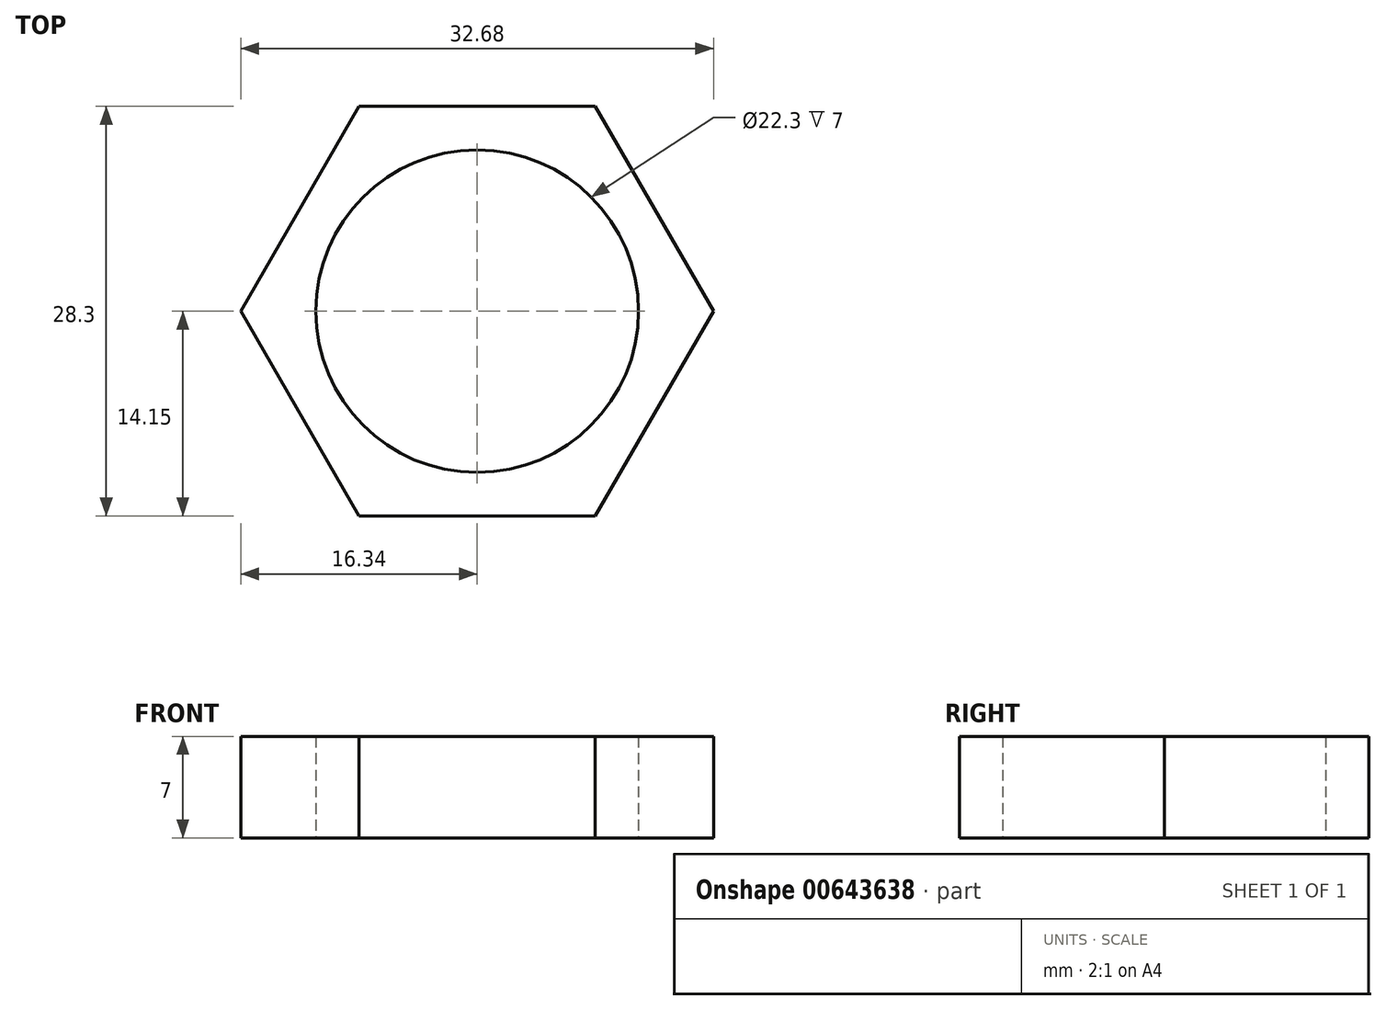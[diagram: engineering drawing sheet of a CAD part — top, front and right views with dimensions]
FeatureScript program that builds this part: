
annotation { "Feature Type Name" : "Feature", "Feature Type Description" : "" }
export const myFeature = defineFeature(function(context is Context, id is Id, definition is map)
    precondition{}
    {
        {
            var Q0;
            Q0=qCreatedBy(makeId("Top.planeOp"),FACE);
            var sketch = newSketch(context, id + "F0", { "sketchPlane" : qUnion([Q0])});
            skCircle(sketch, "E0", {"center": v(0, 0) * mm, "radius": 11.15 * mm});
            skLineSegment(sketch, "E1.0", {"start": v(-8.17, 14.15) * mm, "end": v(8.17, 14.15) * mm});
            skLineSegment(sketch, "E1.1", {"start": v(8.17, 14.15) * mm, "end": v(16.34, 0) * mm});
            skLineSegment(sketch, "E1.2", {"start": v(16.34, 0) * mm, "end": v(8.17, -14.15) * mm});
            skLineSegment(sketch, "E1.3", {"start": v(8.17, -14.15) * mm, "end": v(-8.17, -14.15) * mm});
            skLineSegment(sketch, "E1.4", {"start": v(-8.17, -14.15) * mm, "end": v(-16.34, 0) * mm});
            skLineSegment(sketch, "E1.5", {"start": v(-16.34, 0) * mm, "end": v(-8.17, 14.15) * mm});
            skPoint(sketch, "E1.0.midPoint", {"position": v(0, 14.15) * mm});
            skPoint(sketch, "E2", {"position": v(12.25, -7.07) * mm});
            skCircle(sketch, "E3.cCircle", {"center": v(24.5, -14.15) * mm, "radius": 14.15 * mm, "construction": true});
            skLineSegment(sketch, "E3.0", {"start": v(8.17, -14.15) * mm, "end": v(16.34, 0) * mm});
            skLineSegment(sketch, "E3.1", {"start": v(16.34, 0) * mm, "end": v(32.68, 0) * mm});
            skLineSegment(sketch, "E3.2", {"start": v(32.68, 0) * mm, "end": v(40.85, -14.15) * mm});
            skLineSegment(sketch, "E3.3", {"start": v(40.85, -14.15) * mm, "end": v(32.68, -28.3) * mm});
            skLineSegment(sketch, "E3.4", {"start": v(32.68, -28.3) * mm, "end": v(16.34, -28.3) * mm});
            skLineSegment(sketch, "E3.5", {"start": v(16.34, -28.3) * mm, "end": v(8.17, -14.15) * mm});
            skPoint(sketch, "E4", {"position": v(-12.25, -7.08) * mm});
            skCircle(sketch, "E5.cCircle", {"center": v(-24.5, -14.15) * mm, "radius": 14.15 * mm, "construction": true});
            skLineSegment(sketch, "E5.0", {"start": v(-16.34, 0) * mm, "end": v(-8.17, -14.15) * mm});
            skLineSegment(sketch, "E5.1", {"start": v(-8.17, -14.15) * mm, "end": v(-16.34, -28.3) * mm});
            skLineSegment(sketch, "E5.2", {"start": v(-16.34, -28.3) * mm, "end": v(-32.68, -28.3) * mm});
            skLineSegment(sketch, "E5.3", {"start": v(-32.68, -28.3) * mm, "end": v(-40.85, -14.15) * mm});
            skLineSegment(sketch, "E5.4", {"start": v(-40.85, -14.15) * mm, "end": v(-32.68, 0) * mm});
            skLineSegment(sketch, "E5.5", {"start": v(-32.68, 0) * mm, "end": v(-16.34, 0) * mm});
            skCircle(sketch, "E6.cCircle", {"center": v(0, 28.3) * mm, "radius": 14.15 * mm, "construction": true});
            skLineSegment(sketch, "E6.0", {"start": v(8.17, 14.15) * mm, "end": v(-8.17, 14.15) * mm});
            skLineSegment(sketch, "E6.1", {"start": v(-8.17, 14.15) * mm, "end": v(-16.34, 28.3) * mm});
            skLineSegment(sketch, "E6.2", {"start": v(-16.34, 28.3) * mm, "end": v(-8.17, 42.45) * mm});
            skLineSegment(sketch, "E6.3", {"start": v(-8.17, 42.45) * mm, "end": v(8.17, 42.45) * mm});
            skLineSegment(sketch, "E6.4", {"start": v(8.17, 42.45) * mm, "end": v(16.34, 28.3) * mm});
            skLineSegment(sketch, "E6.5", {"start": v(16.34, 28.3) * mm, "end": v(8.17, 14.15) * mm});
            skLineSegment(sketch, "E7", {"start": v(36.76, -21.23) * mm, "end": v(29.5, -17.03) * mm, "construction": true});
            skPoint(sketch, "E8.0.midPoint", {"position": v(36.76, -21.23) * mm});
            skLineSegment(sketch, "E9", {"start": v(0, 42.45) * mm, "end": v(0, 34.05) * mm, "construction": true});
            skPoint(sketch, "E10.0.midPoint", {"position": v(0, 42.45) * mm});
            skLineSegment(sketch, "E11", {"start": v(-36.76, -21.23) * mm, "end": v(-29.5, -17.03) * mm, "construction": true});
            skLineSegment(sketch, "E12.0", {"start": v(-33.15, -27.49) * mm, "end": v(-40.38, -14.96) * mm});
            skPoint(sketch, "E12.0.midPoint", {"position": v(-36.76, -21.23) * mm});
            skCircle(sketch, "E13.cCircle", {"center": v(0, 34.05) * mm, "radius": 8.4 * mm, "construction": true});
            skLineSegment(sketch, "E13.0", {"start": v(-4.85, 42.45) * mm, "end": v(4.85, 42.45) * mm});
            skLineSegment(sketch, "E13.1", {"start": v(4.85, 42.45) * mm, "end": v(9.7, 34.05) * mm});
            skLineSegment(sketch, "E13.2", {"start": v(9.7, 34.05) * mm, "end": v(4.85, 25.66) * mm});
            skLineSegment(sketch, "E13.3", {"start": v(4.85, 25.66) * mm, "end": v(-4.85, 25.66) * mm});
            skLineSegment(sketch, "E13.4", {"start": v(-4.85, 25.66) * mm, "end": v(-9.7, 34.05) * mm});
            skLineSegment(sketch, "E13.5", {"start": v(-9.7, 34.05) * mm, "end": v(-4.85, 42.45) * mm});
            skCircle(sketch, "E14.cCircle", {"center": v(29.5, -17.03) * mm, "radius": 8.4 * mm, "construction": true});
            skLineSegment(sketch, "E14.0", {"start": v(39.19, -17.03) * mm, "end": v(34.34, -25.42) * mm});
            skLineSegment(sketch, "E14.1", {"start": v(34.34, -25.42) * mm, "end": v(24.65, -25.42) * mm});
            skLineSegment(sketch, "E14.2", {"start": v(24.65, -25.42) * mm, "end": v(19.8, -17.03) * mm});
            skLineSegment(sketch, "E14.3", {"start": v(19.8, -17.03) * mm, "end": v(24.65, -8.63) * mm});
            skLineSegment(sketch, "E14.4", {"start": v(24.65, -8.63) * mm, "end": v(34.34, -8.63) * mm});
            skLineSegment(sketch, "E14.5", {"start": v(34.34, -8.63) * mm, "end": v(39.19, -17.03) * mm});
            skCircle(sketch, "E15.cCircle", {"center": v(-29.5, -17.03) * mm, "radius": 8.4 * mm, "construction": true});
            skLineSegment(sketch, "E15.0", {"start": v(-34.34, -25.42) * mm, "end": v(-39.19, -17.03) * mm});
            skLineSegment(sketch, "E15.1", {"start": v(-39.19, -17.03) * mm, "end": v(-34.34, -8.63) * mm});
            skLineSegment(sketch, "E15.2", {"start": v(-34.34, -8.63) * mm, "end": v(-24.65, -8.63) * mm});
            skLineSegment(sketch, "E15.3", {"start": v(-24.65, -8.63) * mm, "end": v(-19.8, -17.03) * mm});
            skLineSegment(sketch, "E15.4", {"start": v(-19.8, -17.03) * mm, "end": v(-24.65, -25.42) * mm});
            skLineSegment(sketch, "E15.5", {"start": v(-24.65, -25.42) * mm, "end": v(-34.34, -25.42) * mm});
            skSolve(sketch);
        }
        {
            var Q0;
            Q0=makeQuery(id+"F0.imprint","IMPRINT",FACE,{"disambiguationData":[TD([[makeQuery(id+"F0.imprint","IMPRINT",EDGE,{"derivedFrom":sQuery(id+"F0.wireOp",EDGE,"E6.0")}),-1.0]])]});
            var Q1;
            Q1=makeQuery(id+"F0.imprint","IMPRINT",FACE,{"disambiguationData":[TD([[makeQuery(id+"F0.imprint","IMPRINT",EDGE,{"derivedFrom":sQuery(id+"F0.wireOp",EDGE,"E0")}),-1.0]])]});
            var Q2;
            Q2=makeQuery(id+"F0.imprint","IMPRINT",FACE,{"disambiguationData":[TD([[makeQuery(id+"F0.imprint","IMPRINT",EDGE,{"derivedFrom":sQuery(id+"F0.wireOp",EDGE,"E5.0")}),-1.0]])]});
            var Q3;
            Q3=makeQuery(id+"F0.imprint","IMPRINT",FACE,{"disambiguationData":[TD([[makeQuery(id+"F0.imprint","IMPRINT",EDGE,{"derivedFrom":sQuery(id+"F0.wireOp",EDGE,"E3.0")}),-1.0]])]});
            extrude(context, id + "F1", {"entities" : qUnion([Q0, Q1, Q2, Q3]), "depth" : 7 * mm, "offsetDistance" : 25 * mm});
        }
    });
